# Revit family: ВКПІ Л М_Eng
name_source: partatom
category: Mechanical Equipment
units: mm (PartAtom-declared; Revit-internal decimal feet)

## family parameters
Always vertical = Yes
Classification = None
Cut with Voids When Loaded = No
Part Type = Normal
Room Calculation Point = No
Round Connector Dimension = Use Diameter
Shared = No
Work Plane-Based = No

## types (16) — shared parameters
00_20_Manufacturer = Vents
00_20_Name = Centrifugal fan
Casing Material = Steel, galvanized
Description = For rectangular channels
Frequency = 50 Hz
Load Classification = HVAC
Maintenance zone material = <By Category>
Manufacturer = Vents
Temperature of moving air = -25...+50 °C
URL = https://ventilation-system.com
w = 50 mm  [stored 0.164042 ft]
zero-valued in all types: Default Elevation

## per-type parameters (varying)
- VKPI 300х150 M1 EC: 00_20_Type=VKPI 300х150 M1 EC; Amperage=1 A; B=300 mm; B1=320 mm; B2=340 mm; B3=364 mm; Be=129 mm; Bracket=No; Electrical box=Yes; F=364 mm; H=150 mm  [stored 0.492126 ft]; H1=170 mm  [stored 0.557743 ft]; H2=190 mm  [stored 0.62336 ft]; H3=271 mm  [stored 0.889108 ft]; Handle=No; He=250 mm  [stored 0.82021 ft]; Height=271 mm  [stored 0.889108 ft]; K=50 mm  [stored 0.164042 ft]; L=370 mm; Le=19 mm; Length=370 mm; Maximum Air Flow=565.0 m³/h; Number of Fase=1; Power=97 W; Sound pressure level at 3 m distance=29 dBA; Voltage=230 V; Weight=10.30 kg; Width=364 mm; a=40 mm  [stored 0.131234 ft]; b3=91 mm  [stored 0.298556 ft]; h=41 mm  [stored 0.134514 ft]; h1=271 mm  [stored 0.889108 ft]; k=123 mm; l=120 mm  [stored 0.393701 ft]; l1=70 mm  [stored 0.229659 ft]; Сonnector=No
- VKPI 1000х500 L3 EC: 00_20_Type=VKPI 300х150 M1 EC; Amperage=5 A; B=1000 mm; B1=1020 mm; B2=1040 mm; B3=1064 mm; Be=532 mm; Bracket=Yes; Electrical box=No; F=1183 mm; H=500 mm; H1=520 mm; H2=540 mm; H3=814 mm; Handle=Yes; He=546 mm; Height=814 mm; K=850 mm; L=1052 mm; Le=263 mm  [stored 0.862861 ft]; Length=1052 mm; Maximum Air Flow=11190.0 m³/h; Number of Fase=3; Power=3429 W; Sound pressure level at 3 m distance=47 dBA; Voltage=400 V; Weight=130.00 kg; Width=1064 mm; a=60 mm  [stored 0.19685 ft]; b3=266 mm  [stored 0.872703 ft]; h=46 mm; h1=550 mm; k=425 mm; l=470 mm; l1=420 mm; Сonnector=Yes
- VKPI 300х150 L1 EC: 00_20_Type=VKPI 300х150 L1 EC; Amperage=1 A; B=300 mm; B1=320 mm; B2=340 mm; B3=364 mm; Be=129 mm; Bracket=No; Electrical box=Yes; F=364 mm; H=150 mm  [stored 0.492126 ft]; H1=170 mm  [stored 0.557743 ft]; H2=190 mm  [stored 0.62336 ft]; H3=271 mm  [stored 0.889108 ft]; Handle=No; He=250 mm  [stored 0.82021 ft]; Height=271 mm  [stored 0.889108 ft]; K=50 mm  [stored 0.164042 ft]; L=370 mm; Le=19 mm; Length=370 mm; Maximum Air Flow=665.0 m³/h; Number of Fase=1; Power=101 W; Sound pressure level at 3 m distance=30 dBA; Voltage=230 V; Weight=10.30 kg; Width=364 mm; a=40 mm  [stored 0.131234 ft]; b3=91 mm  [stored 0.298556 ft]; h=41 mm  [stored 0.134514 ft]; h1=271 mm  [stored 0.889108 ft]; k=123 mm; l=120 mm  [stored 0.393701 ft]; l1=70 mm  [stored 0.229659 ft]; Сonnector=No
- VKPI 400х200 M1 EC: 00_20_Type=VKPI 400х200 M1 EC; Amperage=1 A; B=400 mm; B1=420 mm; B2=440 mm; B3=464 mm; Be=154 mm; Bracket=No; Electrical box=Yes; F=464 mm; H=200 mm  [stored 0.656168 ft]; H1=220 mm  [stored 0.721785 ft]; H2=240 mm  [stored 0.787402 ft]; H3=322 mm; Handle=No; He=301 mm; Height=322 mm; K=50 mm  [stored 0.164042 ft]; L=460 mm; Le=19 mm; Length=460 mm; Maximum Air Flow=810.0 m³/h; Number of Fase=1; Power=91 W; Sound pressure level at 3 m distance=33 dBA; Voltage=230 V; Weight=15.10 kg; Width=464 mm; a=40 mm  [stored 0.131234 ft]; b3=116 mm  [stored 0.380577 ft]; h=41 mm  [stored 0.134514 ft]; h1=322 mm; k=153 mm; l=170 mm  [stored 0.557743 ft]; l1=120 mm  [stored 0.393701 ft]; Сonnector=No
- VKPI 400х200 L1 EC: 00_20_Type=VKPI 400х200 L1 EC; Amperage=1 A; B=400 mm; B1=420 mm; B2=440 mm; B3=464 mm; Be=154 mm; Bracket=No; Electrical box=Yes; F=464 mm; H=200 mm  [stored 0.656168 ft]; H1=220 mm  [stored 0.721785 ft]; H2=240 mm  [stored 0.787402 ft]; H3=322 mm; Handle=No; He=301 mm; Height=322 mm; K=50 mm  [stored 0.164042 ft]; L=460 mm; Le=19 mm; Length=460 mm; Maximum Air Flow=1190.0 m³/h; Number of Fase=1; Power=192 W; Sound pressure level at 3 m distance=30 dBA; Voltage=230 V; Weight=16.80 kg; Width=464 mm; a=40 mm  [stored 0.131234 ft]; b3=116 mm  [stored 0.380577 ft]; h=41 mm  [stored 0.134514 ft]; h1=322 mm; k=153 mm; l=170 mm  [stored 0.557743 ft]; l1=120 mm  [stored 0.393701 ft]; Сonnector=No
- VKPI 500х250 M1 EC: 00_20_Type=VKPI 500х250 M1 EC; Amperage=2 A; B=500 mm; B1=520 mm; B2=540 mm; B3=564 mm; Be=179 mm; Bracket=No; Electrical box=Yes; F=564 mm; H=250 mm  [stored 0.82021 ft]; H1=270 mm  [stored 0.885827 ft]; H2=290 mm  [stored 0.951444 ft]; H3=373 mm; Handle=No; He=352 mm; Height=373 mm; K=50 mm  [stored 0.164042 ft]; L=560 mm; Le=19 mm; Length=560 mm; Maximum Air Flow=1590.0 m³/h; Number of Fase=1; Power=252 W; Sound pressure level at 3 m distance=34 dBA; Voltage=230 V; Weight=25.50 kg; Width=564 mm; a=40 mm  [stored 0.131234 ft]; b3=141 mm; h=42 mm  [stored 0.137795 ft]; h1=373 mm; k=187 mm; l=220 mm  [stored 0.721785 ft]; l1=170 mm  [stored 0.557743 ft]; Сonnector=No
- VKPI 500х250 L1 EC: 00_20_Type=VKPI 500х250 L1 EC; Amperage=4 A; B=500 mm; B1=520 mm; B2=540 mm; B3=564 mm; Be=179 mm; Bracket=No; Electrical box=Yes; F=564 mm; H=250 mm  [stored 0.82021 ft]; H1=270 mm  [stored 0.885827 ft]; H2=290 mm  [stored 0.951444 ft]; H3=373 mm; Handle=No; He=352 mm; Height=373 mm; K=50 mm  [stored 0.164042 ft]; L=560 mm; Le=19 mm; Length=560 mm; Maximum Air Flow=2480.0 m³/h; Number of Fase=1; Power=555 W; Sound pressure level at 3 m distance=51 dBA; Voltage=230 V; Weight=27.70 kg; Width=564 mm; a=40 mm  [stored 0.131234 ft]; b3=141 mm; h=42 mm  [stored 0.137795 ft]; h1=373 mm; k=187 mm; l=220 mm  [stored 0.721785 ft]; l1=170 mm  [stored 0.557743 ft]; Сonnector=No
- VKPI 500х300 L1 EC: 00_20_Type=VKPI 500х300 L1 EC; Amperage=3 A; B=500 mm; B1=520 mm; B2=540 mm; B3=564 mm; Be=179 mm; Bracket=No; Electrical box=Yes; F=564 mm; H=300 mm; H1=320 mm; H2=340 mm; H3=424 mm; Handle=No; He=403 mm; Height=424 mm; K=50 mm  [stored 0.164042 ft]; L=560 mm; Le=19 mm; Length=560 mm; Maximum Air Flow=3230.0 m³/h; Number of Fase=1; Power=445 W; Sound pressure level at 3 m distance=43 dBA; Voltage=230 V; Weight=29.00 kg; Width=564 mm; a=40 mm  [stored 0.131234 ft]; b3=141 mm; h=42 mm  [stored 0.137795 ft]; h1=424 mm; k=187 mm; l=220 mm  [stored 0.721785 ft]; l1=170 mm  [stored 0.557743 ft]; Сonnector=No
- VKPI 600х300 M1 EC: 00_20_Type=VKPI 600х300 M1 EC; Amperage=2 A; B=600 mm; B1=620 mm; B2=640 mm; B3=664 mm; Be=332 mm; Bracket=Yes; Electrical box=No; F=783 mm; H=300 mm; H1=320 mm; H2=340 mm; H3=574 mm; Handle=Yes; He=339 mm; Height=574 mm; K=450 mm; L=752 mm; Le=188 mm  [stored 0.616798 ft]; Length=752 mm; Maximum Air Flow=2545.0 m³/h; Number of Fase=1; Power=326 W; Sound pressure level at 3 m distance=34 dBA; Voltage=230 V; Weight=52.90 kg; Width=664 mm; a=60 mm  [stored 0.19685 ft]; b3=166 mm  [stored 0.544619 ft]; h=39 mm  [stored 0.127953 ft]; h1=350 mm; k=225 mm  [stored 0.738189 ft]; l=270 mm  [stored 0.885827 ft]; l1=220 mm  [stored 0.721785 ft]; Сonnector=Yes
- VKPI 600х350 M1 EC: 00_20_Type=VKPI 600х350 M1 EC; Amperage=3 A; B=600 mm; B1=620 mm; B2=640 mm; B3=664 mm; Be=332 mm; Bracket=Yes; Electrical box=No; F=783 mm; H=350 mm; H1=370 mm; H2=390 mm; H3=664 mm; Handle=Yes; He=396 mm; Height=664 mm; K=450 mm; L=752 mm; Le=188 mm  [stored 0.616798 ft]; Length=752 mm; Maximum Air Flow=2815.0 m³/h; Number of Fase=1; Power=361 W; Sound pressure level at 3 m distance=38 dBA; Voltage=230 V; Weight=56.60 kg; Width=664 mm; a=60 mm  [stored 0.19685 ft]; b3=166 mm  [stored 0.544619 ft]; h=46 mm; h1=400 mm; k=225 mm  [stored 0.738189 ft]; l=270 mm  [stored 0.885827 ft]; l1=220 mm  [stored 0.721785 ft]; Сonnector=Yes
- VKPI 600х350 L3 EC: 00_20_Type=VKPI 600х350 L3 EC; Amperage=2 A; B=600 mm; B1=620 mm; B2=640 mm; B3=664 mm; Be=332 mm; Bracket=Yes; Electrical box=No; F=783 mm; H=350 mm; H1=370 mm; H2=390 mm; H3=664 mm; Handle=Yes; He=396 mm; Height=664 mm; K=450 mm; L=752 mm; Le=188 mm  [stored 0.616798 ft]; Length=752 mm; Maximum Air Flow=4290.0 m³/h; Number of Fase=3; Power=1308 W; Sound pressure level at 3 m distance=40 dBA; Voltage=400 V; Weight=59.30 kg; Width=664 mm; a=60 mm  [stored 0.19685 ft]; b3=166 mm  [stored 0.544619 ft]; h=46 mm; h1=400 mm; k=225 mm  [stored 0.738189 ft]; l=270 mm  [stored 0.885827 ft]; l1=220 mm  [stored 0.721785 ft]; Сonnector=Yes
- VKPI 700х400 M1 EC: 00_20_Type=VKPI 700х400 M1 EC; Amperage=3 A; B=700 mm; B1=720 mm; B2=740 mm; B3=764 mm; Be=382 mm; Bracket=Yes; Electrical box=No; F=883 mm; H=400 mm; H1=420 mm; H2=440 mm; H3=714 mm; Handle=Yes; He=446 mm; Height=714 mm; K=742 mm; L=882 mm; Le=221 mm; Length=882 mm; Maximum Air Flow=5710.0 m³/h; Number of Fase=1; Power=795 W; Sound pressure level at 3 m distance=37 dBA; Voltage=230 V; Weight=82.60 kg; Width=764 mm; a=60 mm  [stored 0.19685 ft]; b3=191 mm  [stored 0.62664 ft]; h=46 mm; h1=450 mm; k=371 mm; l=320 mm; l1=270 mm  [stored 0.885827 ft]; Сonnector=Yes
- VKPI 700х400 L3 EC: 00_20_Type=VKPI 700х400 L3 EC; Amperage=3 A; B=700 mm; B1=720 mm; B2=740 mm; B3=764 mm; Be=382 mm; Bracket=Yes; Electrical box=No; F=883 mm; H=400 mm; H1=420 mm; H2=440 mm; H3=714 mm; Handle=Yes; He=446 mm; Height=714 mm; K=742 mm; L=882 mm; Le=221 mm; Length=882 mm; Maximum Air Flow=6810.0 m³/h; Number of Fase=3; Power=2748 W; Sound pressure level at 3 m distance=43 dBA; Voltage=400 V; Weight=83.40 kg; Width=764 mm; a=60 mm  [stored 0.19685 ft]; b3=191 mm  [stored 0.62664 ft]; h=46 mm; h1=450 mm; k=371 mm; l=320 mm; l1=270 mm  [stored 0.885827 ft]; Сonnector=Yes
- VKPI 800х500 M3 EC: 00_20_Type=VKPI 800х500 M3 EC; Amperage=2 A; B=800 mm; B1=820 mm; B2=840 mm; B3=864 mm; Be=432 mm; Bracket=Yes; Electrical box=No; F=983 mm; H=500 mm; H1=520 mm; H2=540 mm; H3=814 mm; Handle=Yes; He=546 mm; Height=814 mm; K=797 mm; L=937 mm; Le=234 mm; Length=937 mm; Maximum Air Flow=8395.0 m³/h; Number of Fase=3; Power=2025 W; Sound pressure level at 3 m distance=43 dBA; Voltage=400 V; Weight=108.40 kg; Width=864 mm; a=60 mm  [stored 0.19685 ft]; b3=216 mm  [stored 0.708661 ft]; h=46 mm; h1=550 mm; k=399 mm; l=370 mm; l1=320 mm; Сonnector=Yes
- VKPI 800х500 L3 EC: 00_20_Type=VKPI 800х500 L3 EC; Amperage=3 A; B=800 mm; B1=820 mm; B2=840 mm; B3=864 mm; Be=432 mm; Bracket=Yes; Electrical box=No; F=983 mm; H=500 mm; H1=520 mm; H2=540 mm; H3=814 mm; Handle=Yes; He=546 mm; Height=814 mm; K=797 mm; L=937 mm; Le=234 mm; Length=937 mm; Maximum Air Flow=8535.0 m³/h; Number of Fase=3; Power=2925 W; Sound pressure level at 3 m distance=42 dBA; Voltage=400 V; Weight=99.80 kg; Width=864 mm; a=60 mm  [stored 0.19685 ft]; b3=216 mm  [stored 0.708661 ft]; h=46 mm; h1=550 mm; k=399 mm; l=370 mm; l1=320 mm; Сonnector=Yes
- VKPI 900х500 L3 EC: 00_20_Type=VKPI 900х500 L3 EC; Amperage=5 A; B=900 mm; B1=920 mm; B2=940 mm; B3=964 mm; Be=482 mm; Bracket=Yes; Electrical box=No; F=1083 mm; H=500 mm; H1=520 mm; H2=540 mm; H3=814 mm; Handle=Yes; He=546 mm; Height=814 mm; K=850 mm; L=1052 mm; Le=263 mm  [stored 0.862861 ft]; Length=1052 mm; Maximum Air Flow=11190.0 m³/h; Number of Fase=3; Power=3429 W; Sound pressure level at 3 m distance=47 dBA; Voltage=400 V; Weight=120.00 kg; Width=964 mm; a=60 mm  [stored 0.19685 ft]; b3=241 mm  [stored 0.790682 ft]; h=46 mm; h1=550 mm; k=425 mm; l=420 mm; l1=370 mm; Сonnector=Yes

note: [stored X ft] marks values corroborated as IEEE doubles in the binary element streams (Revit-internal decimal feet)
